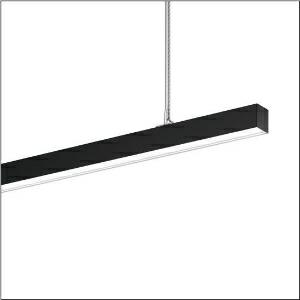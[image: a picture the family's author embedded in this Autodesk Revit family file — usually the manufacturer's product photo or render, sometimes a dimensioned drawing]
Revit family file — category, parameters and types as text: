
# Revit family: silica_r__21_51mx30dc49bb_d1ca
name_source: partatom
category: Lighting Fixtures
units: mm (PartAtom-declared; Revit-internal decimal feet)

## family parameters
Cut with Voids When Loaded = No
Host = Face
Light Source = No
Part Type = Normal
Room Calculation Point = No
Round Connector Dimension = Use Diameter
Shared = No

## types (1)
- --- (1 x LED, 10520 lm, 64.1 W, 4000K)
    Apparent Load = 64 VA
    CIE Flux Codes = 47 79 96 57 100
    Color Rendering = 80
    Color Temperature = 4000K
    Default Elevation = 1800 mm
    Description = Silica® 21, office luminaire, primary optical cover: cover, of PMMA, opal, light emission: direct/indirect distribution, primary light characteristic: symmetric, installation type: suspended mounting, LED, rated luminous flux: 10.520lm, luminous efficacy: 164lm/W, light colour: 840, colour temperature: 4000K, control gear: DALI 2, with terminal, 3+2-pole, max. 2.5mm², mains connection: 220..240V, AC, 50/60Hz, rated input power: 64.1W, luminaire housing, of aluminium, matt jet black (RAL 9005), length: 3.004mm, width: 53mm, height: 53mm, protection rating (complete): IP20, insulation class (complete): insulation class I (protective earthing), certification: CE, permissible operating ambient temperature: 0..+35°C, standard: EN 50419, packaging unit: 1 piece
    Height = 53 mm
    Lamp = 1 x LED
    Lamp Light Flux = 10520 lm
    Lamp Power = 64.1 W
    Lamp count = 1
    Length = 3004 mm
    Luminous efficacy = 164 lm/W
    Manufacturer = Siteco
    ModVariant = No
    Model = 51MX30DC49BB
    Mounting Place = Ceiling
    Mounting Type = Pendant
    Number of Poles = 1
    OnlyDefault = Yes
    Power Factor = 1
    Product Name = Silica® 21
    Product group = office luminaire | ceiling pendant
    ProductGroupID = 904
    Protection Class = Protection class I
    Protection Degree = IP 20
    RLX_Detail_Level = 1
    RLX_Emergency_Light_Flux = 0 lm
    RLX_Emergency_Type = 0
    RLX_Emergency_Type_DB = No
    RlxData = <blob elided: 26085 chars, md5=ca1c2155>
    Socket = socket
    Standby Power = 0 W
    System Light Flux = 10520 lm
    System Power = 64 W
    Type Comments = factory setting: luminous flux: 100 % | dim-lin: 254 | 218 mA
    Type Image = l_1335856.jpg
    URL = http://relux.com
    VarID = @adj_117268
    Voltage = 0 V
    Weight = 0.00 kg
    Width = 53 mm

## geometry (parser evidence)
native form markers: Blend x4, Sweep x12
no freeform markers — native parametric forms only
